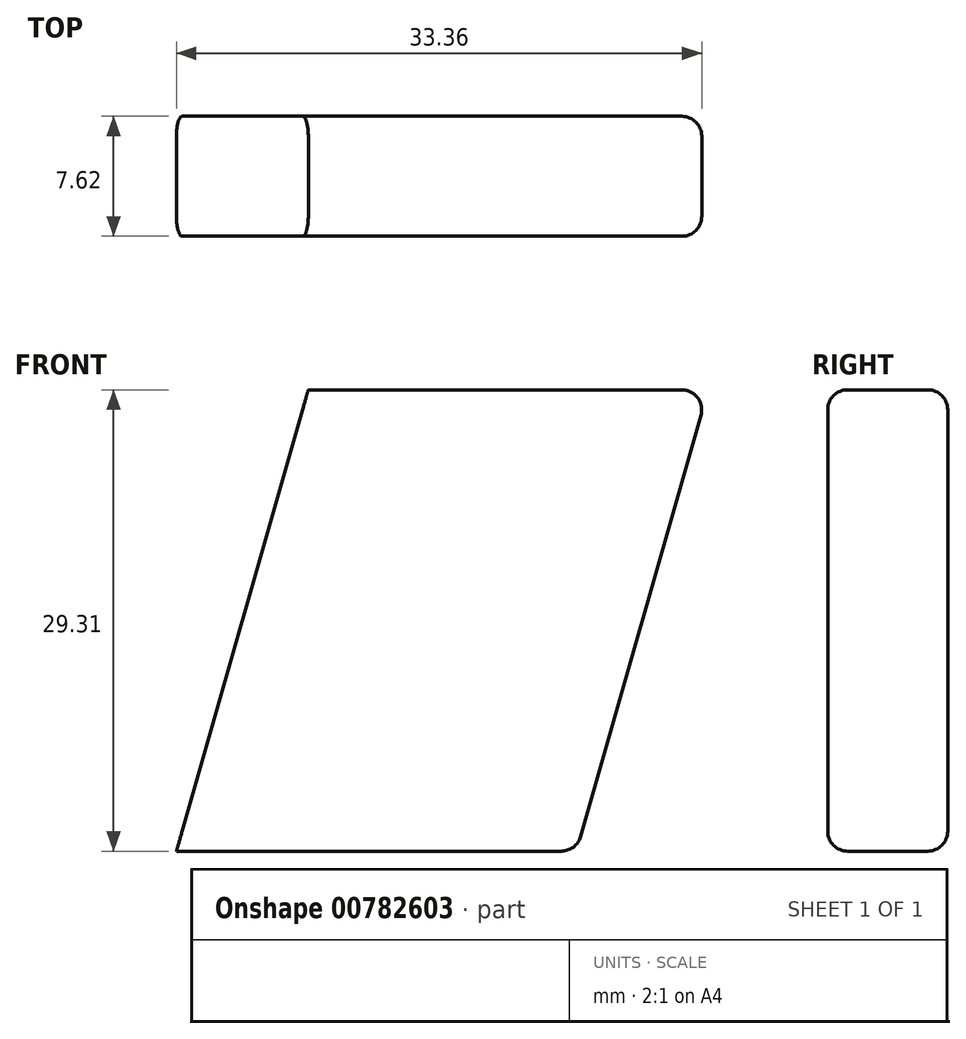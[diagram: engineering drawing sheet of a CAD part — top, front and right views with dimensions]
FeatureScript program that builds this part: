
annotation { "Feature Type Name" : "Feature", "Feature Type Description" : "" }
export const myFeature = defineFeature(function(context is Context, id is Id, definition is map)
    precondition{}
    {
        {
            var Q0;
            Q0=qCreatedBy(makeId("Front.planeOp"),FACE);
            var sketch = newSketch(context, id + "F0", { "sketchPlane" : qUnion([Q0])});
            skLineSegment(sketch, "E0", {"start": v(0, 0) * mm, "end": v(0, 104.14) * mm, "construction": true});
            skLineSegment(sketch, "E1", {"start": v(0, 104.14) * mm, "end": v(47, 104.14) * mm, "construction": true});
            skFitSpline(sketch, "E2", {"points": [v(47, 104.14) * mm, v(30.48, 0) * mm], "startDerivative": vector(7.11, -113.99) * mm, "endDerivative": vector(-26.77, -49.74) * mm});
            skLineSegment(sketch, "E3", {"start": v(47, 104.14) * mm, "end": v(41.91, 104.14) * mm, "construction": true});
            skLineSegment(sketch, "E4", {"start": v(0, 0) * mm, "end": v(0, 5.08) * mm, "construction": true});
            skFitSpline(sketch, "E5", {"points": [v(0, 5.08) * mm, v(25.4, 0) * mm], "startDerivative": vector(75.58, 0.88) * mm, "endDerivative": vector(11.48, -3.19) * mm});
            skLineSegment(sketch, "E6", {"start": v(25.4, 0) * mm, "end": v(30.48, 0) * mm});
            skFitSpline(sketch, "E7.0", {"points": [v(41.92, 103.82) * mm, v(42.2, 99.22) * mm, v(42.41, 89.6) * mm, v(41.74, 74.55) * mm, v(40.23, 59.4) * mm, v(38.05, 44.73) * mm, v(35.35, 31.06) * mm, v(32.3, 18.96) * mm, v(29.61, 10.64) * mm, v(27.5, 5.4) * mm, v(26.49, 3.3) * mm, v(26, 2.4) * mm]});
            skLineSegment(sketch, "E7.1", {"start": v(26.74, 5.08) * mm, "end": v(27.31, 5.08) * mm});
            skFitSpline(sketch, "E7.2", {"points": [v(-0.06, 10.16) * mm, v(2.7, 10.2) * mm, v(7.55, 10.15) * mm, v(13.22, 9.81) * mm, v(17.58, 9.24) * mm, v(20.38, 8.58) * mm, v(22.26, 7.92) * mm, v(23.52, 7.36) * mm, v(24.63, 6.74) * mm, v(25.56, 6.1) * mm, v(26.18, 5.58) * mm, v(26.57, 5.24) * mm, v(26.8, 5.02) * mm, v(26.98, 4.86) * mm, v(27.08, 4.77) * mm, v(27.12, 4.73) * mm, v(27.14, 4.7) * mm, v(27.15, 4.7) * mm, v(27.16, 4.7) * mm, v(27.16, 4.7) * mm, v(27.16, 4.7) * mm, v(27.17, 4.7) * mm, v(27.17, 4.7) * mm, v(27.16, 4.7) * mm, v(27.17, 4.68) * mm, v(27.18, 4.68) * mm, v(27.2, 4.66) * mm, v(27.22, 4.65) * mm, v(27.23, 4.64) * mm]});
            skArc(sketch, "E8", {"start": v(46.99, 104.14) * mm, "mid": v(44.3, 106.42) * mm, "end": v(41.92, 103.82) * mm});
            skLineSegment(sketch, "E9", {"start": v(-0.06, 10.16) * mm, "end": v(0, 5.08) * mm});
            skSolve(sketch);
        }
        {
            var Q0;
            Q0=sQuery(id+"F0.wireOp",EDGE,"E7.2");
            var Q1;
            Q1=sQuery(id+"F0.wireOp",EDGE,"E7.1");
            var Q2;
            Q2=sQuery(id+"F0.wireOp",EDGE,"E7.0");
            var Q3;
            Q3=sQuery(id+"F0.wireOp",EDGE,"E8");
            var Q4;
            Q4=sQuery(id+"F0.wireOp",EDGE,"E2");
            var Q5;
            Q5=sQuery(id+"F0.wireOp",EDGE,"E6");
            var Q6;
            Q6=sQuery(id+"F0.wireOp",EDGE,"E5");
            var Q7;
            Q7=sQuery(id+"F0.wireOp",EDGE,"E9");
            revolve(context, id + "F1", {"bodyType" : ToolBodyType.SURFACE, "surfaceOperationType" : NewSurfaceOperationType.NEW, "surfaceEntities" : qUnion([Q0, Q1, Q2, Q3, Q4, Q5, Q6]), "axis" : qUnion([Q7]), "revolveType" : RevolveType.FULL});
        }
        {
            var Q0;
            Q0=qCreatedBy(makeId("Front.planeOp"),FACE);
            var sketch = newSketch(context, id + "F2", { "sketchPlane" : qUnion([Q0])});
            skLineSegment(sketch, "E10", {"start": v(42, 47.97) * mm, "end": v(33.63, 18.66) * mm});
            skLineSegment(sketch, "E11", {"start": v(33.63, 18.66) * mm, "end": v(59.03, 18.66) * mm});
            skLineSegment(sketch, "E12", {"start": v(42, 47.97) * mm, "end": v(67.4, 47.97) * mm});
            skLineSegment(sketch, "E13", {"start": v(67.4, 47.97) * mm, "end": v(59.03, 18.66) * mm});
            skSolve(sketch);
        }
        {
            var Q0;
            Q0=makeQuery(id+"F2.imprint","IMPRINT",FACE,{"disambiguationData":[TD([[makeQuery(id+"F2.imprint","IMPRINT",EDGE,{"derivedFrom":sQuery(id+"F2.wireOp",EDGE,"E10")}),1.0]])]});
            extrude(context, id + "F3", {"entities" : qUnion([Q0]), "endBound" : BoundingType.SYMMETRIC, "depth" : 7.62 * mm, "offsetDistance" : 25.4 * mm});
        }
        {
            var Q0;
            Q0=makeQuery(id+"F3.opExtrude","CAP_EDGE",EDGE,{"disambiguationData":[OSD([sQuery(id+"F2.wireOp",EDGE,"E12")])],"isStart":false});
            var Q1;
            Q1=makeQuery(id+"F3.opExtrude","CAP_EDGE",EDGE,{"disambiguationData":[OSD([sQuery(id+"F2.wireOp",EDGE,"E13")])],"isStart":false});
            var Q2;
            Q2=makeQuery(id+"F3.opExtrude","CAP_EDGE",EDGE,{"disambiguationData":[OSD([sQuery(id+"F2.wireOp",EDGE,"E11")])],"isStart":false});
            var Q3;
            Q3=makeQuery(id+"F3.opExtrude","CAP_EDGE",EDGE,{"disambiguationData":[OSD([sQuery(id+"F2.wireOp",EDGE,"E13")])],"isStart":true});
            var Q4;
            Q4=makeQuery(id+"F3.opExtrude","CAP_EDGE",EDGE,{"disambiguationData":[OSD([sQuery(id+"F2.wireOp",EDGE,"E12")])],"isStart":true});
            var Q5;
            Q5=makeQuery(id+"F3.opExtrude","CAP_EDGE",EDGE,{"disambiguationData":[OSD([sQuery(id+"F2.wireOp",EDGE,"E11")])],"isStart":true});
            var Q6;
            Q6=makeQuery(id+"F3.opExtrude","SWEPT_EDGE",EDGE,{"disambiguationData":[OSD([sQuery(id+"F2.wireOp",EDGE,"E12"),sQuery(id+"F2.wireOp",EDGE,"E13")])]});
            var Q7;
            Q7=makeQuery(id+"F3.opExtrude","SWEPT_EDGE",EDGE,{"disambiguationData":[OSD([sQuery(id+"F2.wireOp",EDGE,"E11"),sQuery(id+"F2.wireOp",EDGE,"E13")])]});
            fillet(context, id + "F4", {"entities" : qUnion([Q0, Q1, Q2, Q3, Q4, Q5, Q6, Q7]), "radius" : 1.27 * mm, "tangentPropagation" : true, "allowEdgeOverflow" : false});
        }
    });
